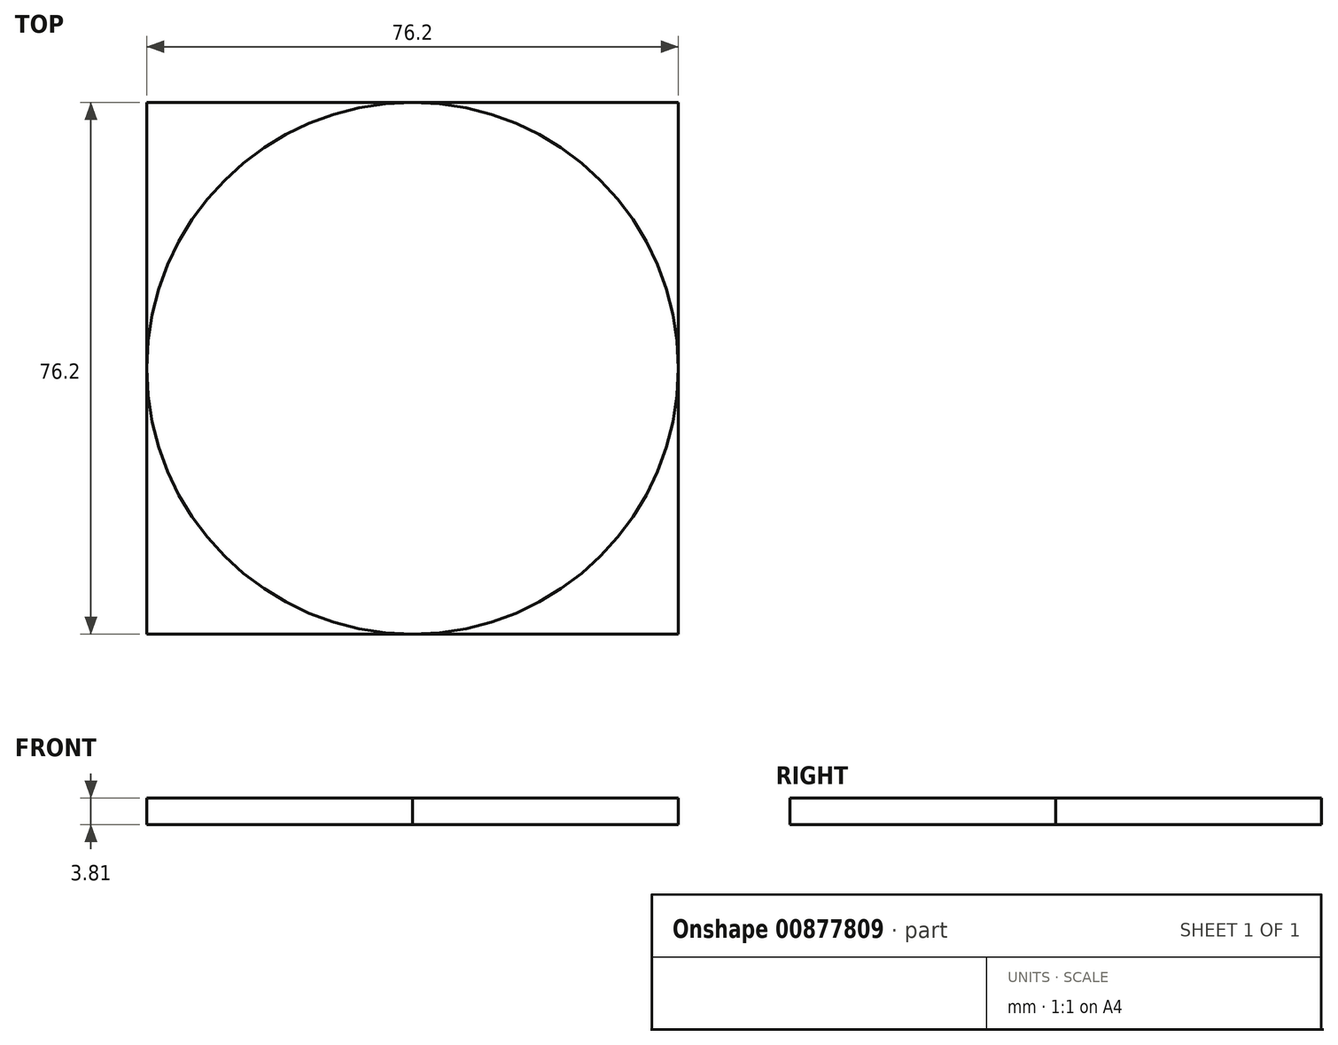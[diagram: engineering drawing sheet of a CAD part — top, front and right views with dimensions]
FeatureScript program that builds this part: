
annotation { "Feature Type Name" : "Feature", "Feature Type Description" : "" }
export const myFeature = defineFeature(function(context is Context, id is Id, definition is map)
    precondition{}
    {
        {
            var Q0;
            Q0=qCreatedBy(makeId("Top.planeOp"),FACE);
            var sketch = newSketch(context, id + "F0", { "sketchPlane" : qUnion([Q0])});
            skCircle(sketch, "E0", {"center": v(0, 0) * mm, "radius": 127 * mm});
            skSolve(sketch);
        }
        {
            var Q0;
            Q0=makeQuery(id+"F0.imprint","IMPRINT",FACE,{"disambiguationData":[TD([[makeQuery(id+"F0.imprint","IMPRINT",EDGE,{"derivedFrom":sQuery(id+"F0.wireOp",EDGE,"E0")}),1.0]])]});
            cPlane(context, id + "F1", {"entities" : qUnion([Q0]), "cplaneType" : CPlaneType.OFFSET, "offset" : 254 * mm, "oppositeDirection" : true, "width" : 152.4 * mm, "height" : 152.4 * mm});
        }
        {
            var Q0;
            Q0=qCreatedBy(id+"F1.planeOp",FACE);
            var sketch = newSketch(context, id + "F2", { "sketchPlane" : qUnion([Q0])});
            skCircle(sketch, "E1", {"center": v(0, 0) * mm, "radius": 38.1 * mm});
            skSolve(sketch);
        }
        {
            var Q0;
            Q0=makeQuery(id+"F2.imprint","IMPRINT",FACE,{"disambiguationData":[TD([[makeQuery(id+"F2.imprint","IMPRINT",EDGE,{"derivedFrom":sQuery(id+"F2.wireOp",EDGE,"E1")}),1.0]])]});
            var Q1;
            Q1=makeQuery(id+"F0.imprint","IMPRINT",FACE,{"disambiguationData":[TD([[makeQuery(id+"F0.imprint","IMPRINT",EDGE,{"derivedFrom":sQuery(id+"F0.wireOp",EDGE,"E0")}),1.0]])]});
            var Q2;
            Q2=sQuery(id+"F0.wireOp",EDGE,"E0");
            var Q3;
            Q3=sQuery(id+"F2.wireOp",EDGE,"E1");
            loft(context, id + "F3", {"bodyType" : ToolBodyType.SURFACE, "sheetProfilesArray" : [{ "sheetProfileEntities" : qUnion([Q0]) }, { "sheetProfileEntities" : qUnion([Q1]) }], "wireProfilesArray" : [{ "wireProfileEntities" : qUnion([Q2]) }, { "wireProfileEntities" : qUnion([Q3]) }]});
        }
        {
            var Q0;
            Q0=qCreatedBy(id+"F1.planeOp",FACE);
            var sketch = newSketch(context, id + "F4", { "sketchPlane" : qUnion([Q0])});
            skLineSegment(sketch, "E2.bottom", {"start": v(38.1, 38.1) * mm, "end": v(-38.1, 38.1) * mm});
            skLineSegment(sketch, "E2.top", {"start": v(38.1, -38.1) * mm, "end": v(-38.1, -38.1) * mm});
            skLineSegment(sketch, "E2.left", {"start": v(38.1, 38.1) * mm, "end": v(38.1, -38.1) * mm});
            skLineSegment(sketch, "E2.right", {"start": v(-38.1, 38.1) * mm, "end": v(-38.1, -38.1) * mm});
            skPoint(sketch, "E2.middle", {"position": v(0, 0) * mm});
            skSolve(sketch);
        }
        {
            var Q0;
            Q0=makeQuery(id+"F4.imprint","IMPRINT",FACE,{"disambiguationData":[TD([[makeQuery(id+"F4.imprint","IMPRINT",EDGE,{"derivedFrom":sQuery(id+"F4.wireOp",EDGE,"E2.bottom")}),1.0]])]});
            extrude(context, id + "F5", {"entities" : qUnion([Q0]), "depth" : 3.8 * mm, "offsetDistance" : 25.4 * mm});
        }
        {
            var Q0;
            Q0=makeQuery(id+"F5.opExtrude","CAP_FACE",FACE,{"disambiguationData":[OSD([sQuery(id+"F4.wireOp",EDGE,"E2.bottom"),sQuery(id+"F4.wireOp",EDGE,"E2.top"),sQuery(id+"F4.wireOp",EDGE,"E2.left"),sQuery(id+"F4.wireOp",EDGE,"E2.right")])],"isStart":true});
            var sketch = newSketch(context, id + "F6", { "sketchPlane" : qUnion([Q0])});
            skCircle(sketch, "E3", {"center": v(0, 0) * mm, "radius": 38.1 * mm});
            skSolve(sketch);
        }
        {
            var Q0;
            {var subQ0=sQuery(id+"F6.wireOp",EDGE,"E3");var subQ1=makeQuery(id+"F6.imprint","INTERSECT",VERTEX,{"derivedFrom":[makeQuery(id+"F5.opExtrude","CAP_EDGE",EDGE,{"disambiguationData":[OSD([sQuery(id+"F4.wireOp",EDGE,"E2.top")])],"isStart":true}),subQ0]});Q0=makeQuery(id+"F6.imprint","IMPRINT",FACE,{"disambiguationData":[TD([[makeQuery(id+"F6.imprint","IMPRINT",EDGE,{"disambiguationData":[TD([[subQ1,1.0]])],"derivedFrom":subQ0}),1.0]])]});}
            extrude(context, id + "F7", {"entities" : qUnion([Q0]), "operationType" : NewBodyOperationType.REMOVE, "oppositeDirection" : true, "depth" : 101.35 * mm, "offsetDistance" : 25.4 * mm});
        }
    });
